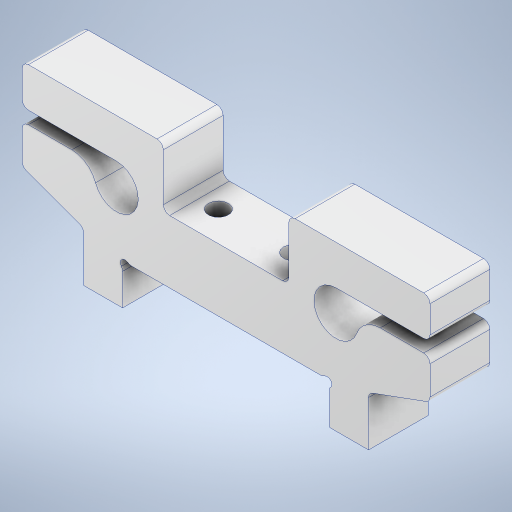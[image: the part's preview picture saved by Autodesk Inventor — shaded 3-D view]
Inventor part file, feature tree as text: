
AUTODESK INVENTOR PART (.ipt)
format: ipt  version: 2024 (Build 280153000, 153)  size: 471,552 bytes
history: native  units: mm
features: sketch x7, extrude x6, fillet x6, projected_geometry x5, mirror x2, hole x1
ambient origin geometry x8: Origin, YZ Plane, XZ Plane, XY Plane, X Axis, Y Axis, Z Axis, Center Point
bodies: Solid1 (feature_tree)
feature tree (27):
  extrude  "Extrusion1"  Depth=33.0mm
  extrude  "Extrusion2"  Depth=65.0mm
  fillet  "Fillet1"  Radius=18.0mm
  mirror  "Mirror1"
  extrude  "Extrusion3"  Depth=9.525mm TaperAngle=0.0deg
  extrude  "Extrusion4"  Depth=2.0mm
  extrude  "Extrusion5"  TaperAngle=0.0deg  [1 undecoded]
  fillet  "Fillet3"  Radius=4.0mm
  fillet  "Fillet4"  Radius=10.0mm
  hole  "Hole1"  [1 undecoded]
  fillet  "Fillet6"  Radius=1.0mm
  fillet  "Fillet7"  Radius=6.285mm
  extrude  "Extrusion6"  TaperAngle=0.0deg  [1 undecoded]
  fillet  "Fillet8"  Radius=1.0mm
  mirror  "Mirror2"
  sketch  "Sketch1"  dims[d0=45.4mm d1=33.0mm]
  sketch  "Sketch2"  dims[d2=6.5mm d3=65.0mm d4=18.0mm]
  projected_geometry  "Projected Loop1"
  sketch  "Sketch3"  dims[d5=5.0mm d6=9.525mm d7=0.0mm]
  projected_geometry  "Projected Loop2"
  sketch  "Sketch4"  dims[d8=2.0mm d9=7.0mm]
  projected_geometry  "Projected Loop3"
  sketch  "Sketch5"  dims[d10=15.0mm d12=0.0mm d13=0.0mm d14=4.0mm d19=10.0mm]
  sketch  "Sketch6"  dims[d20=20.0mm d21=0.0mm d22=0.0mm d24=1.0mm d25=6.285mm]
  projected_geometry  "Projected Loop4"
  sketch  "Sketch7"  dims[d26=6.285mm d27=0.0mm d28=0.0mm d29=1.0mm d30=12.0mm d31=3.2mm d32=6.0mm d33=4.0mm d34=2.0mm d35=90.0deg d36=8.0mm d37=20.594885mm d38=18.65mm d39=12.73mm d40=1.0mm d42=1.0mm d43=19.198622mm d44=19.198622mm d45=10.0mm d46=0.0mm d47=1.0mm d48=1.5mm d49=0.4mm d50=0.4mm d51=0.0mm d52=0.0mm d53=1.0mm]
  projected_geometry  "Projected Loop5"
note: 3 required parameter values undecoded (feature->parameter linkage not recoverable at this tier; creation-order binding heuristic only, values carry confidence <= 0.55)
